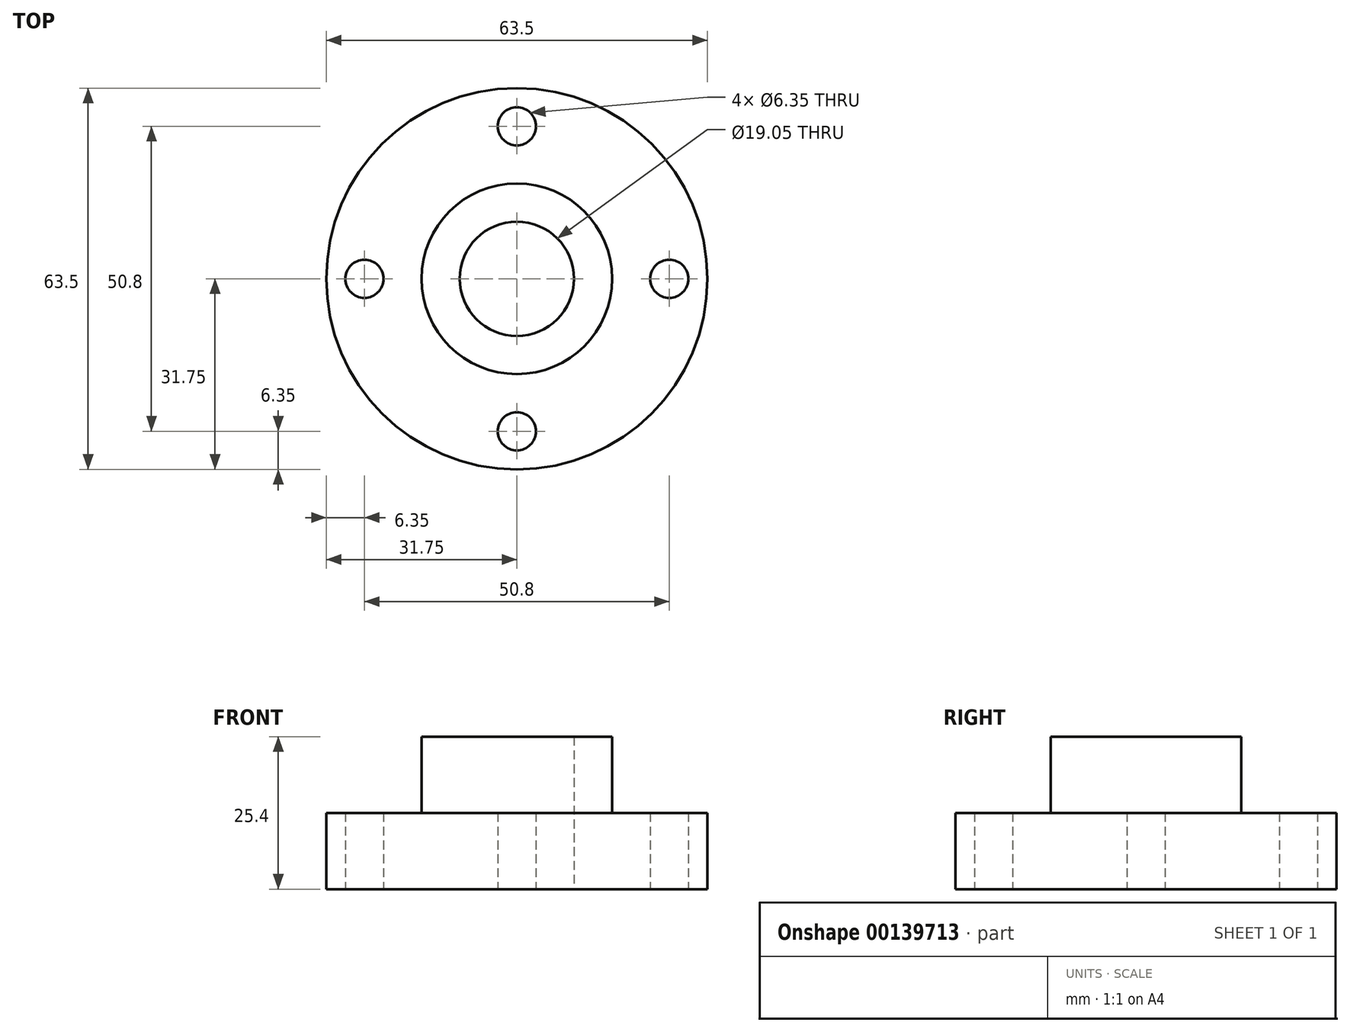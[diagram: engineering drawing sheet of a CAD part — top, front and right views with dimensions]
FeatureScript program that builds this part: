
annotation { "Feature Type Name" : "Feature", "Feature Type Description" : "" }
export const myFeature = defineFeature(function(context is Context, id is Id, definition is map)
    precondition{}
    {
        {
            var Q0;
            Q0=qCreatedBy(makeId("Top.planeOp"),FACE);
            var sketch = newSketch(context, id + "F0", { "sketchPlane" : qUnion([Q0])});
            skCircle(sketch, "E0", {"center": v(0, 0) * mm, "radius": 31.75 * mm});
            skCircle(sketch, "E1", {"center": v(0, 0) * mm, "radius": 25.4 * mm, "construction": true});
            skCircle(sketch, "E2", {"center": v(0, 25.4) * mm, "radius": 3.18 * mm});
            skCircle(sketch, "E3", {"center": v(0, -25.4) * mm, "radius": 3.18 * mm});
            skCircle(sketch, "E4", {"center": v(-25.4, 0) * mm, "radius": 3.18 * mm});
            skCircle(sketch, "E5", {"center": v(25.4, 0) * mm, "radius": 3.18 * mm});
            skSolve(sketch);
        }
        {
            var Q0;
            Q0 = qSketchRegion(id + "F0", true);
            extrude(context, id + "F1", {"entities" : qUnion([Q0]), "depth" : 12.7 * mm});
        }
        {
            var Q0;
            Q0=makeQuery(id+"F1.opExtrude","CAP_FACE",FACE,{"disambiguationData":[OSD([sQuery(id+"F0.wireOp",EDGE,"E0"),sQuery(id+"F0.wireOp",EDGE,"E2"),sQuery(id+"F0.wireOp",EDGE,"E3"),sQuery(id+"F0.wireOp",EDGE,"E4"),sQuery(id+"F0.wireOp",EDGE,"E5")])],"isStart":false});
            var sketch = newSketch(context, id + "F2", { "sketchPlane" : qUnion([Q0])});
            skCircle(sketch, "E6", {"center": v(0, 0) * mm, "radius": 15.88 * mm});
            skCircle(sketch, "E7", {"center": v(0, 0) * mm, "radius": 9.53 * mm});
            skSolve(sketch);
        }
        {
            var Q0;
            Q0 = qSketchRegion(id + "F2", true);
            extrude(context, id + "F3", {"entities" : qUnion([Q0]), "operationType" : NewBodyOperationType.ADD, "depth" : 12.7 * mm});
        }
        {
            var Q0;
            Q0=makeQuery(id+"F3.boolean.opBoolean","SPLIT",FACE,{"disambiguationData":[TD([makeQuery(id+"F3.opExtrude","SWEPT_FACE",FACE,{"disambiguationData":[OSD([sQuery(id+"F2.wireOp",EDGE,"E7")])]})])],"derivedFrom":makeQuery(id+"F1.opExtrude","CAP_FACE",FACE,{"disambiguationData":[OSD([sQuery(id+"F0.wireOp",EDGE,"E0"),sQuery(id+"F0.wireOp",EDGE,"E2"),sQuery(id+"F0.wireOp",EDGE,"E3"),sQuery(id+"F0.wireOp",EDGE,"E4"),sQuery(id+"F0.wireOp",EDGE,"E5")])],"isStart":false})});
            extrude(context, id + "F4", {"entities" : qUnion([Q0]), "operationType" : NewBodyOperationType.REMOVE, "oppositeDirection" : true, "depth" : 25.4 * mm});
        }
    });
